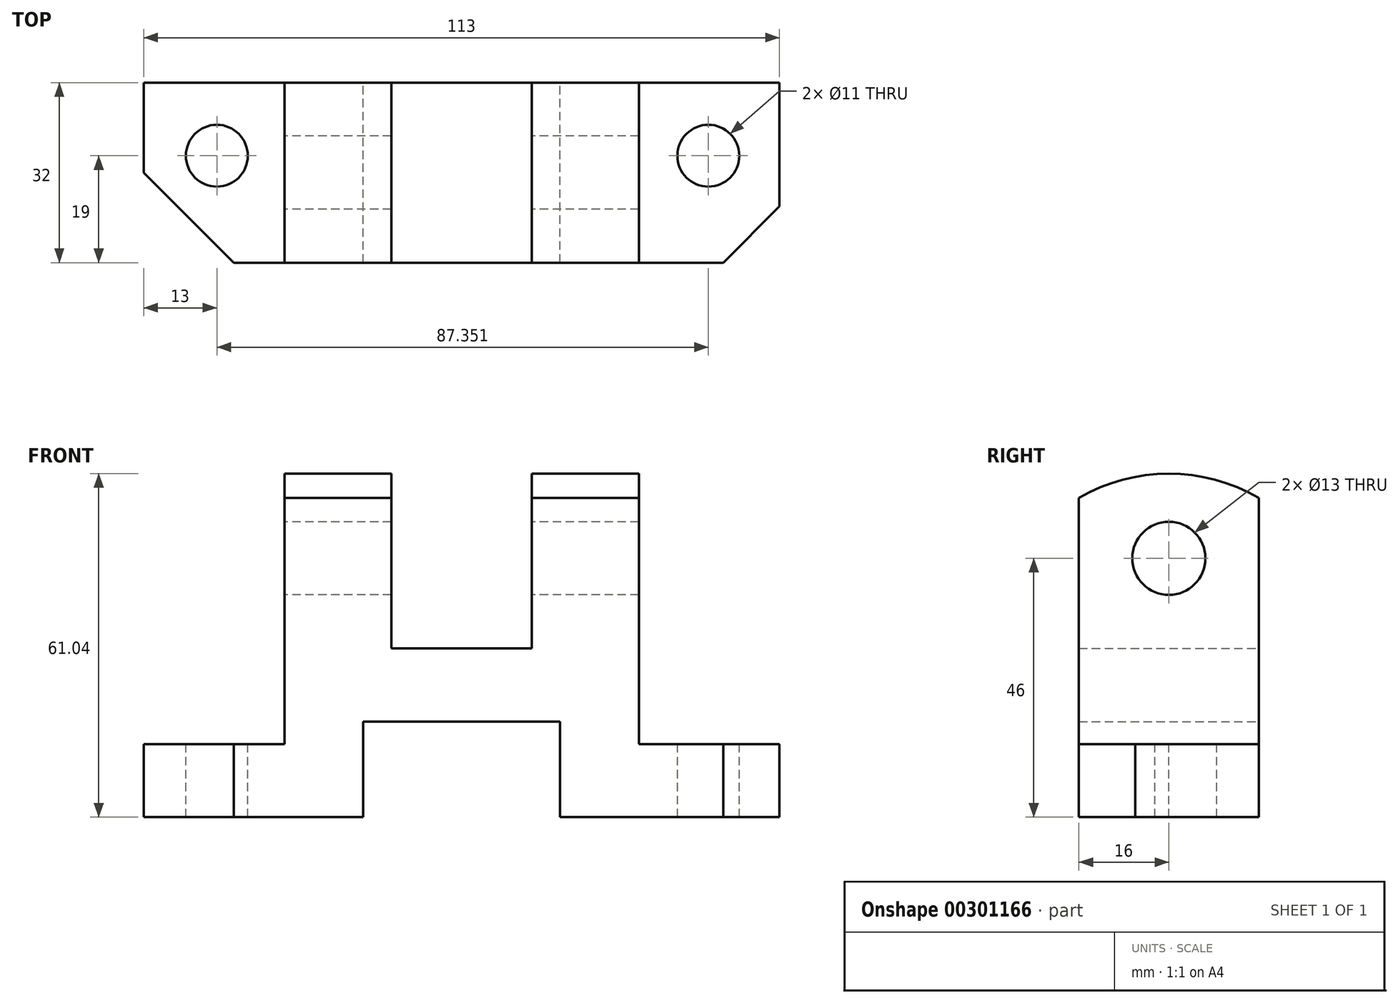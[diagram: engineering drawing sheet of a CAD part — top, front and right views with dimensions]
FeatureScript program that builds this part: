
annotation { "Feature Type Name" : "Feature", "Feature Type Description" : "" }
export const myFeature = defineFeature(function(context is Context, id is Id, definition is map)
    precondition{}
    {
        {
            var Q0;
            Q0=qCreatedBy(makeId("Front.planeOp"),FACE);
            var sketch = newSketch(context, id + "F0", { "sketchPlane" : qUnion([Q0])});
            skLineSegment(sketch, "E0", {"start": v(0, 0) * mm, "end": v(0, -13) * mm});
            skLineSegment(sketch, "E1", {"start": v(113, -13) * mm, "end": v(113, 0) * mm});
            skLineSegment(sketch, "E2", {"start": v(113, 0) * mm, "end": v(88, 0) * mm});
            skLineSegment(sketch, "E3", {"start": v(88, 0) * mm, "end": v(88, 43.75) * mm});
            skLineSegment(sketch, "E4", {"start": v(88, 43.75) * mm, "end": v(69, 43.75) * mm});
            skLineSegment(sketch, "E5", {"start": v(69, 43.75) * mm, "end": v(69, 17) * mm});
            skLineSegment(sketch, "E6", {"start": v(69, 17) * mm, "end": v(44, 17) * mm});
            skLineSegment(sketch, "E7", {"start": v(44, 17) * mm, "end": v(44, 43.75) * mm});
            skLineSegment(sketch, "E8", {"start": v(44, 43.75) * mm, "end": v(25, 43.75) * mm});
            skLineSegment(sketch, "E9", {"start": v(25, 43.75) * mm, "end": v(25, 0) * mm});
            skLineSegment(sketch, "E10", {"start": v(25, 0) * mm, "end": v(0, 0) * mm});
            skLineSegment(sketch, "E11", {"start": v(0, -13) * mm, "end": v(39, -13) * mm});
            skLineSegment(sketch, "E12.top", {"start": v(39, 4) * mm, "end": v(74, 4) * mm});
            skLineSegment(sketch, "E12.left", {"start": v(39, -13) * mm, "end": v(39, 4) * mm});
            skLineSegment(sketch, "E12.right", {"start": v(74, -13) * mm, "end": v(74, 4) * mm});
            skLineSegment(sketch, "E13.trimOffspring", {"start": v(74, -13) * mm, "end": v(113, -13) * mm});
            skSolve(sketch);
        }
        {
            var Q0;
            Q0 = qSketchRegion(id + "F0", true);
            extrude(context, id + "F1", {"entities" : qUnion([Q0]), "depth" : 32 * mm});
        }
        {
            var Q0;
            Q0=qCreatedBy(makeId("Top.planeOp"),FACE);
            var sketch = newSketch(context, id + "F2", { "sketchPlane" : qUnion([Q0])});
            skCircle(sketch, "E14", {"center": v(13, -13) * mm, "radius": 5.5 * mm});
            skCircle(sketch, "E15", {"center": v(100.35, -13) * mm, "radius": 5.5 * mm});
            skLineSegment(sketch, "E16", {"start": v(0, -16) * mm, "end": v(16, -32) * mm});
            skLineSegment(sketch, "E17", {"start": v(0, -16) * mm, "end": v(0, -32) * mm});
            skLineSegment(sketch, "E18", {"start": v(0, -32) * mm, "end": v(16, -32) * mm});
            skLineSegment(sketch, "E19", {"start": v(103, -32) * mm, "end": v(113, -32) * mm});
            skLineSegment(sketch, "E20", {"start": v(113, -32) * mm, "end": v(113, -22) * mm});
            skLineSegment(sketch, "E21", {"start": v(113, -22) * mm, "end": v(103, -32) * mm});
            skPoint(sketch, "E22.start.orphan", {"position": v(10, 0) * mm});
            skPoint(sketch, "E23.end.orphan", {"position": v(0, -10) * mm});
            skPoint(sketch, "E24.start.orphan", {"position": v(103, 0) * mm});
            skSolve(sketch);
        }
        {
            var Q0;
            Q0 = qSketchRegion(id + "F2", true);
            extrude(context, id + "F3", {"entities" : qUnion([Q0]), "operationType" : NewBodyOperationType.REMOVE, "endBound" : BoundingType.THROUGH_ALL, "oppositeDirection" : true, "depth" : 25 * mm});
        }
        {
            var Q0;
            Q0=makeQuery(id+"F1.opExtrude","SWEPT_FACE",FACE,{"disambiguationData":[OSD([sQuery(id+"F0.wireOp",EDGE,"E9")])]});
            var sketch = newSketch(context, id + "F4", { "sketchPlane" : qUnion([Q0])});
            skLineSegment(sketch, "E25", {"start": v(0, 43.75) * mm, "end": v(0, 0) * mm});
            skLineSegment(sketch, "E26", {"start": v(32, 43.75) * mm, "end": v(32, 0) * mm});
            skArc(sketch, "E27", {"start": v(32, 43.75) * mm, "mid": v(16, 48.04) * mm, "end": v(0, 43.75) * mm});
            skCircle(sketch, "E28", {"center": v(16, 33) * mm, "radius": 6.5 * mm});
            skSolve(sketch);
        }
        {
            var Q0;
            Q0=makeQuery(id+"F4.imprint","IMPRINT",FACE,{"disambiguationData":[TD([[makeQuery(id+"F4.imprint","IMPRINT",EDGE,{"derivedFrom":sQuery(id+"F4.wireOp",EDGE,"E27")}),1.0]])]});
            extrude(context, id + "F5", {"entities" : qUnion([Q0]), "operationType" : NewBodyOperationType.ADD, "oppositeDirection" : true, "depth" : 19 * mm});
        }
        {
            var Q0;
            Q0=makeQuery(id+"F4.imprint","IMPRINT",FACE,{"disambiguationData":[TD([[makeQuery(id+"F4.imprint","IMPRINT",EDGE,{"derivedFrom":sQuery(id+"F4.wireOp",EDGE,"E28")}),1.0]])]});
            var Q1;
            Q1=sQuery(id+"F4.wireOp",EDGE,"E28");
            extrude(context, id + "F6", {"entities" : qUnion([Q0]), "operationType" : NewBodyOperationType.REMOVE, "surfaceEntities" : qUnion([Q1]), "endBound" : BoundingType.THROUGH_ALL, "oppositeDirection" : true, "depth" : 25 * mm});
        }
        {
            var Q0;
            Q0=makeQuery(id+"F1.opExtrude","SWEPT_FACE",FACE,{"disambiguationData":[OSD([sQuery(id+"F0.wireOp",EDGE,"E3")])]});
            var sketch = newSketch(context, id + "F7", { "sketchPlane" : qUnion([Q0])});
            skLineSegment(sketch, "E29", {"start": v(-32, 43.75) * mm, "end": v(-32, 0) * mm});
            skLineSegment(sketch, "E30", {"start": v(0, 43.75) * mm, "end": v(0, 0) * mm});
            skArc(sketch, "E31", {"start": v(0, 43.75) * mm, "mid": v(-16, 48.04) * mm, "end": v(-32, 43.75) * mm});
            skSolve(sketch);
        }
        {
            var Q0;
            Q0=makeQuery(id+"F7.imprint","IMPRINT",FACE,{"disambiguationData":[TD([[makeQuery(id+"F7.imprint","IMPRINT",EDGE,{"derivedFrom":sQuery(id+"F7.wireOp",EDGE,"E31")}),1.0]])]});
            extrude(context, id + "F8", {"entities" : qUnion([Q0]), "operationType" : NewBodyOperationType.ADD, "oppositeDirection" : true, "depth" : 19 * mm});
        }
    });
